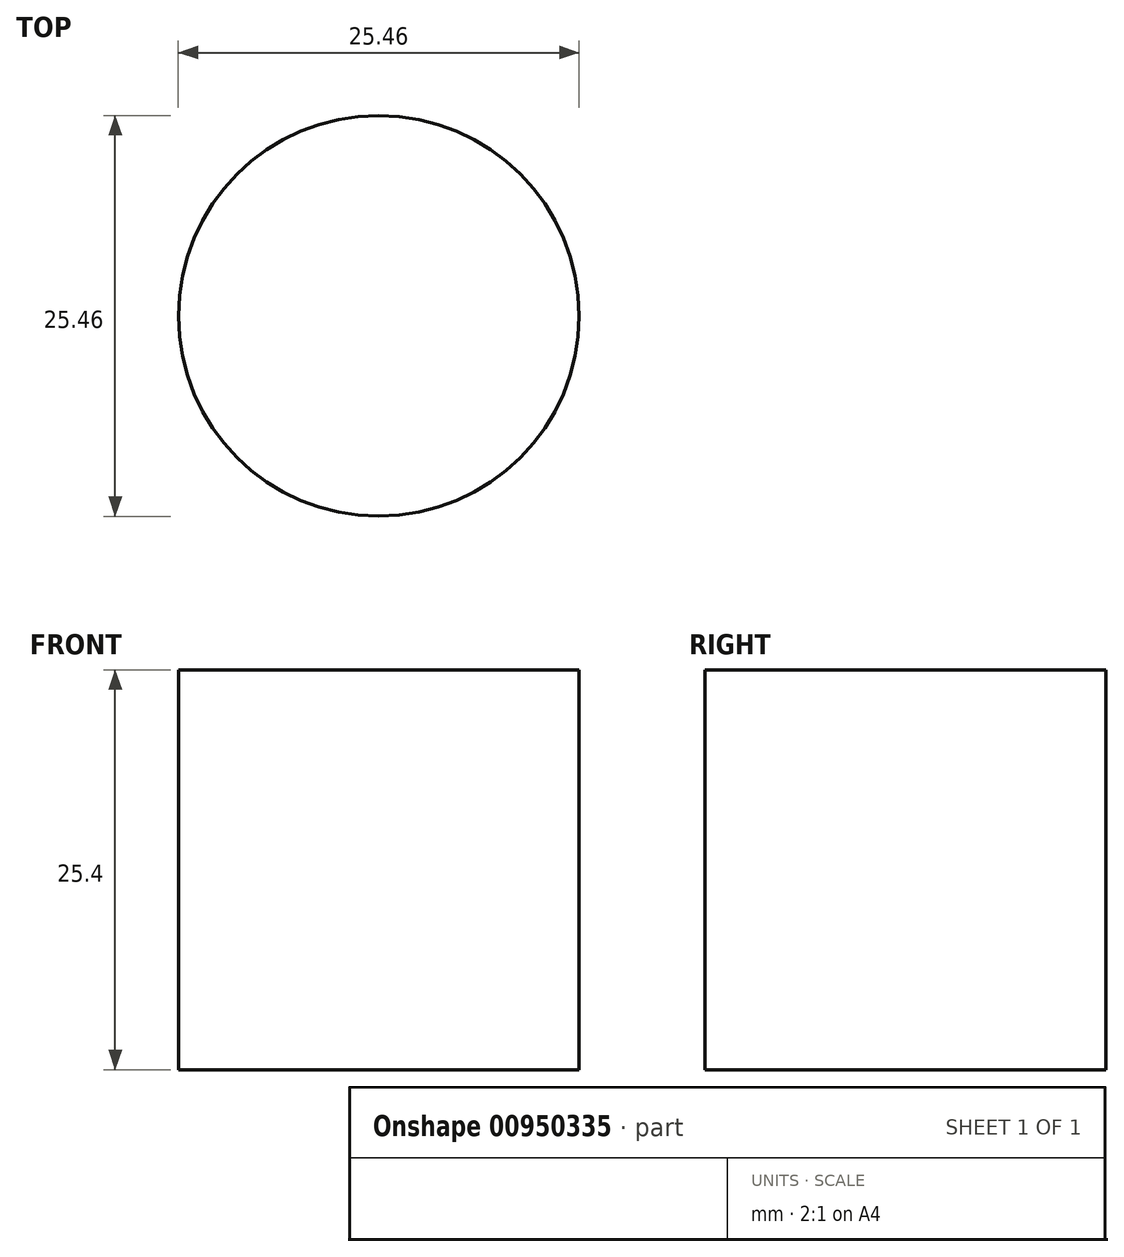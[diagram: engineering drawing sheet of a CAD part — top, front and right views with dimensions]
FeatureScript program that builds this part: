
annotation { "Feature Type Name" : "Feature", "Feature Type Description" : "" }
export const myFeature = defineFeature(function(context is Context, id is Id, definition is map)
    precondition{}
    {
        {
            var Q0;
            Q0=qCreatedBy(makeId("Top.planeOp"),FACE);
            var sketch = newSketch(context, id + "F0", { "sketchPlane" : qUnion([Q0])});
            skCircle(sketch, "E0", {"center": v(0, 0) * mm, "radius": 12.73 * mm});
            skSolve(sketch);
        }
        {
            var Q0;
            Q0=makeQuery(id+"F0.imprint","IMPRINT",FACE,{"disambiguationData":[TD([[makeQuery(id+"F0.imprint","IMPRINT",EDGE,{"derivedFrom":sQuery(id+"F0.wireOp",EDGE,"E0")}),1.0]])]});
            extrude(context, id + "F1", {"entities" : qUnion([Q0]), "depth" : 25.4 * mm, "offsetDistance" : 25.4 * mm});
        }
    });
